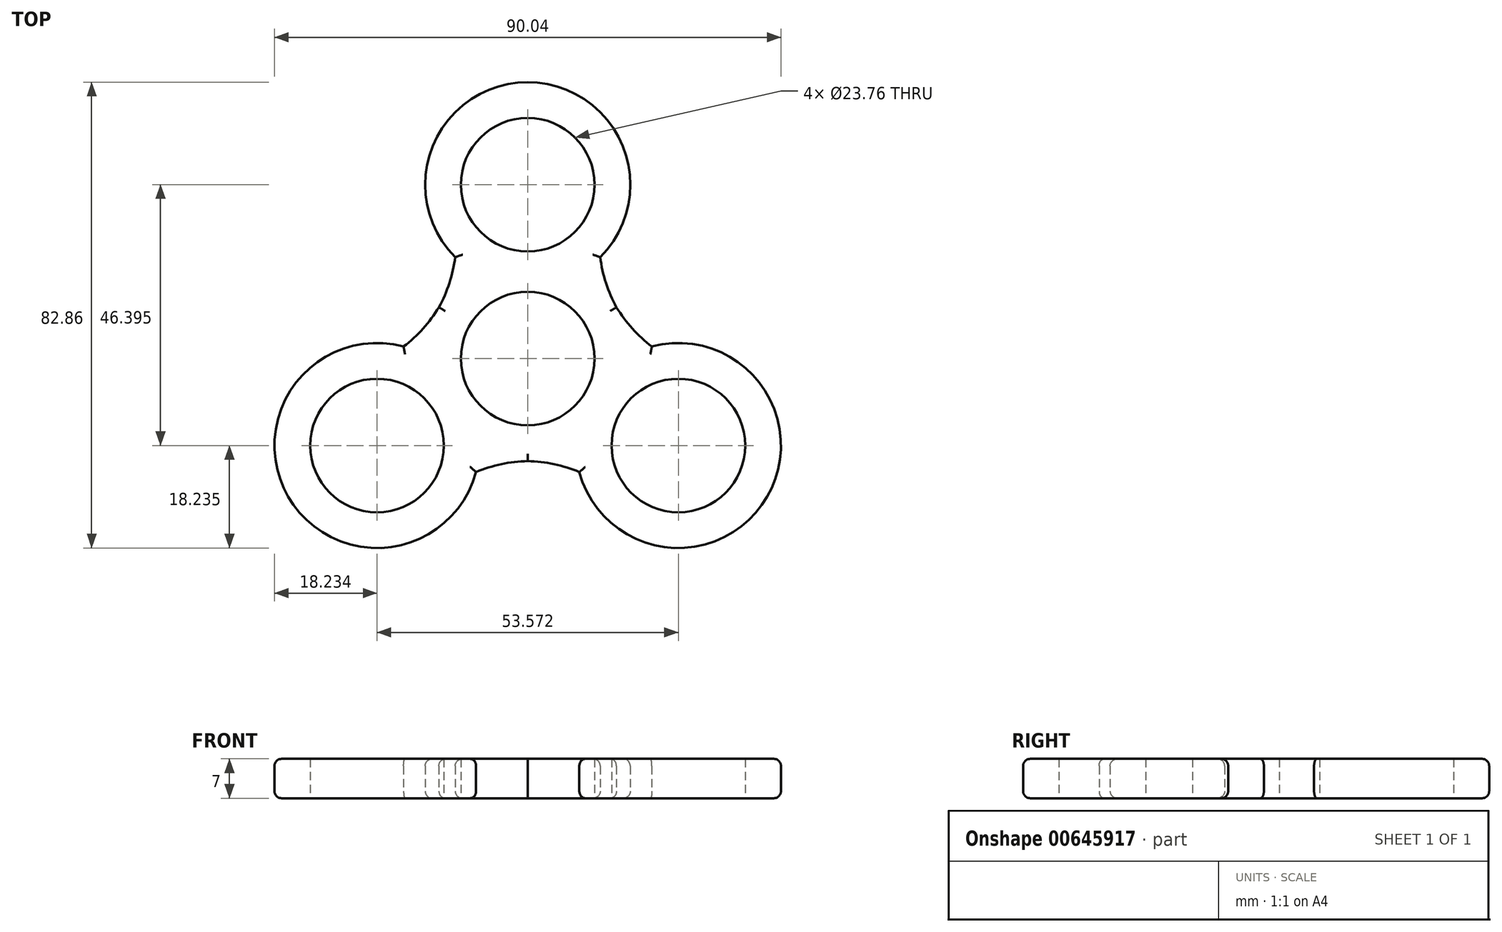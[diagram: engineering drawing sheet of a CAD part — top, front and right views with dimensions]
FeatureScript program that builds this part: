
annotation { "Feature Type Name" : "Feature", "Feature Type Description" : "" }
export const myFeature = defineFeature(function(context is Context, id is Id, definition is map)
    precondition{}
    {
        {
            var Q0;
            Q0=qCreatedBy(makeId("Top.planeOp"),FACE);
            var sketch = newSketch(context, id + "F0", { "sketchPlane" : qUnion([Q0])});
            skCircle(sketch, "E0", {"center": v(0, 0) * mm, "radius": 11.88 * mm});
            skCircle(sketch, "E1", {"center": v(0, 0) * mm, "radius": 18.23 * mm});
            skLineSegment(sketch, "E2", {"start": v(0, 0) * mm, "end": v(0, 18.23) * mm});
            skLineSegment(sketch, "E3", {"start": v(0, 0) * mm, "end": v(15.79, -9.11) * mm});
            skLineSegment(sketch, "E4", {"start": v(0, 0) * mm, "end": v(-15.79, -9.12) * mm});
            skLineSegment(sketch, "E5", {"start": v(0, 18.23) * mm, "end": v(0, 30.93) * mm});
            skCircle(sketch, "E6", {"center": v(0, 30.93) * mm, "radius": 11.88 * mm});
            skCircle(sketch, "E7", {"center": v(0, 30.93) * mm, "radius": 18.23 * mm});
            skLineSegment(sketch, "E8", {"start": v(0, 0) * mm, "end": v(0, -18.23) * mm});
            skLineSegment(sketch, "E9", {"start": v(0, 0) * mm, "end": v(15.79, 9.12) * mm});
            skLineSegment(sketch, "E10", {"start": v(0, 0) * mm, "end": v(-15.79, 9.12) * mm});
            skLineSegment(sketch, "E11", {"start": v(0, 30.93) * mm, "end": v(12.9, 18.04) * mm});
            skLineSegment(sketch, "E12", {"start": v(0, 30.93) * mm, "end": v(-12.9, 18.04) * mm});
            skArc(sketch, "E13", {"start": v(12.9, 18.04) * mm, "mid": v(13.92, 13.44) * mm, "end": v(15.79, 9.11) * mm});
            skArc(sketch, "E14", {"start": v(-15.79, 9.11) * mm, "mid": v(-13.92, 13.44) * mm, "end": v(-12.9, 18.04) * mm});
            skCircle(sketch, "E15.1.0", {"center": v(-26.79, -15.46) * mm, "radius": 11.88 * mm});
            skCircle(sketch, "E15.1.1", {"center": v(-26.79, -15.46) * mm, "radius": 18.23 * mm});
            skArc(sketch, "E15.1.2", {"start": v(-22.07, 2.14) * mm, "mid": v(-18.6, 5.34) * mm, "end": v(-15.79, 9.12) * mm});
            skArc(sketch, "E15.1.3", {"start": v(0, -18.23) * mm, "mid": v(-4.68, -18.78) * mm, "end": v(-9.18, -20.18) * mm});
            skCircle(sketch, "E15.2.0", {"center": v(26.79, -15.46) * mm, "radius": 11.88 * mm});
            skCircle(sketch, "E15.2.1", {"center": v(26.79, -15.46) * mm, "radius": 18.23 * mm});
            skArc(sketch, "E15.2.2", {"start": v(9.18, -20.18) * mm, "mid": v(4.68, -18.78) * mm, "end": v(0, -18.23) * mm});
            skArc(sketch, "E15.2.3", {"start": v(15.79, 9.11) * mm, "mid": v(18.6, 5.34) * mm, "end": v(22.07, 2.14) * mm});
            skSolve(sketch);
        }
        {
            var Q0;
            {var subQ0=sQuery(id+"F0.wireOp",EDGE,"E12");var subQ1=sQuery(id+"F0.wireOp",EDGE,"E6");var subQ2=makeQuery(id+"F0.imprint","INTERSECT",VERTEX,{"derivedFrom":[subQ1,subQ0]});Q0=makeQuery(id+"F0.imprint","IMPRINT",FACE,{"disambiguationData":[TD([[makeQuery(id+"F0.imprint","IMPRINT",EDGE,{"disambiguationData":[TD([[subQ2,1.0]])],"derivedFrom":subQ1}),-1.0]])]});}
            var Q1;
            {var subQ3=sQuery(id+"F0.wireOp",EDGE,"E14");Q1=makeQuery(id+"F0.imprint","IMPRINT",FACE,{"disambiguationData":[TD([[makeQuery(id+"F0.imprint","IMPRINT",EDGE,{"derivedFrom":subQ3}),-1.0]])]});}
            var Q2;
            {var subQ3=sQuery(id+"F0.wireOp",EDGE,"E13");Q2=makeQuery(id+"F0.imprint","IMPRINT",FACE,{"disambiguationData":[TD([[makeQuery(id+"F0.imprint","IMPRINT",EDGE,{"derivedFrom":subQ3}),-1.0]])]});}
            var Q3;
            {var subQ0=sQuery(id+"F0.wireOp",EDGE,"E2");var subQ1=sQuery(id+"F0.wireOp",EDGE,"E0");var subQ2=makeQuery(id+"F0.imprint","INTERSECT",VERTEX,{"derivedFrom":[subQ1,subQ0]});Q3=makeQuery(id+"F0.imprint","IMPRINT",FACE,{"disambiguationData":[TD([[makeQuery(id+"F0.imprint","IMPRINT",EDGE,{"disambiguationData":[TD([[subQ2,1.0]])],"derivedFrom":subQ1}),-1.0]])]});}
            var Q4;
            {var subQ0=sQuery(id+"F0.wireOp",EDGE,"E2");var subQ1=sQuery(id+"F0.wireOp",EDGE,"E0");var subQ2=makeQuery(id+"F0.imprint","INTERSECT",VERTEX,{"derivedFrom":[subQ1,subQ0]});Q4=makeQuery(id+"F0.imprint","IMPRINT",FACE,{"disambiguationData":[TD([[makeQuery(id+"F0.imprint","IMPRINT",EDGE,{"disambiguationData":[TD([[subQ2,-1.0]])],"derivedFrom":subQ1}),-1.0]])]});}
            var Q5;
            {var subQ0=sQuery(id+"F0.wireOp",EDGE,"E10");var subQ1=sQuery(id+"F0.wireOp",EDGE,"E0");var subQ2=makeQuery(id+"F0.imprint","INTERSECT",VERTEX,{"derivedFrom":[subQ1,subQ0]});Q5=makeQuery(id+"F0.imprint","IMPRINT",FACE,{"disambiguationData":[TD([[makeQuery(id+"F0.imprint","IMPRINT",EDGE,{"disambiguationData":[TD([[subQ2,-1.0]])],"derivedFrom":subQ1}),-1.0]])]});}
            var Q6;
            {var subQ0=sQuery(id+"F0.wireOp",EDGE,"E4");var subQ1=sQuery(id+"F0.wireOp",EDGE,"E0");var subQ2=makeQuery(id+"F0.imprint","INTERSECT",VERTEX,{"derivedFrom":[subQ1,subQ0]});Q6=makeQuery(id+"F0.imprint","IMPRINT",FACE,{"disambiguationData":[TD([[makeQuery(id+"F0.imprint","IMPRINT",EDGE,{"disambiguationData":[TD([[subQ2,-1.0]])],"derivedFrom":subQ1}),-1.0]])]});}
            var Q7;
            {var subQ0=sQuery(id+"F0.wireOp",EDGE,"E8");var subQ1=sQuery(id+"F0.wireOp",EDGE,"E0");var subQ2=makeQuery(id+"F0.imprint","INTERSECT",VERTEX,{"derivedFrom":[subQ1,subQ0]});Q7=makeQuery(id+"F0.imprint","IMPRINT",FACE,{"disambiguationData":[TD([[makeQuery(id+"F0.imprint","IMPRINT",EDGE,{"disambiguationData":[TD([[subQ2,-1.0]])],"derivedFrom":subQ1}),-1.0]])]});}
            var Q8;
            {var subQ0=sQuery(id+"F0.wireOp",EDGE,"E9");var subQ1=sQuery(id+"F0.wireOp",EDGE,"E0");var subQ2=makeQuery(id+"F0.imprint","INTERSECT",VERTEX,{"derivedFrom":[subQ1,subQ0]});Q8=makeQuery(id+"F0.imprint","IMPRINT",FACE,{"disambiguationData":[TD([[makeQuery(id+"F0.imprint","IMPRINT",EDGE,{"disambiguationData":[TD([[subQ2,1.0]])],"derivedFrom":subQ1}),-1.0]])]});}
            var Q9;
            {var subQ0=sQuery(id+"F0.wireOp",EDGE,"E15.2.2");Q9=makeQuery(id+"F0.imprint","IMPRINT",FACE,{"disambiguationData":[TD([[makeQuery(id+"F0.imprint","IMPRINT",EDGE,{"derivedFrom":subQ0}),-1.0]])]});}
            var Q10;
            Q10=makeQuery(id+"F0.imprint","IMPRINT",FACE,{"disambiguationData":[TD([[makeQuery(id+"F0.imprint","IMPRINT",EDGE,{"derivedFrom":sQuery(id+"F0.wireOp",EDGE,"E15.2.0")}),-1.0]])]});
            var Q11;
            {var subQ0=sQuery(id+"F0.wireOp",EDGE,"E15.1.2");Q11=makeQuery(id+"F0.imprint","IMPRINT",FACE,{"disambiguationData":[TD([[makeQuery(id+"F0.imprint","IMPRINT",EDGE,{"derivedFrom":subQ0}),-1.0]])]});}
            var Q12;
            Q12=makeQuery(id+"F0.imprint","IMPRINT",FACE,{"disambiguationData":[TD([[makeQuery(id+"F0.imprint","IMPRINT",EDGE,{"derivedFrom":sQuery(id+"F0.wireOp",EDGE,"E15.1.0")}),-1.0]])]});
            var Q13;
            {var subQ5=sQuery(id+"F0.wireOp",EDGE,"E5");var subQ7=sQuery(id+"F0.wireOp",EDGE,"E6");var subQ8=makeQuery(id+"F0.imprint","INTERSECT",VERTEX,{"derivedFrom":[subQ5,subQ7]});Q13=makeQuery(id+"F0.imprint","IMPRINT",FACE,{"disambiguationData":[TD([[makeQuery(id+"F0.imprint","IMPRINT",EDGE,{"disambiguationData":[TD([[subQ8,1.0]])],"derivedFrom":subQ7}),-1.0]])]});}
            var Q14;
            {var subQ5=sQuery(id+"F0.wireOp",EDGE,"E6");var subQ6=sQuery(id+"F0.wireOp",EDGE,"E5");var subQ7=makeQuery(id+"F0.imprint","INTERSECT",VERTEX,{"derivedFrom":[subQ6,subQ5]});Q14=makeQuery(id+"F0.imprint","IMPRINT",FACE,{"disambiguationData":[TD([[makeQuery(id+"F0.imprint","IMPRINT",EDGE,{"disambiguationData":[TD([[subQ7,-1.0]])],"derivedFrom":subQ5}),-1.0]])]});}
            var Q15;
            {var subQ1=sQuery(id+"F0.wireOp",EDGE,"E1");var subQ3=sQuery(id+"F0.wireOp",EDGE,"E7");var subQ4=makeQuery(id+"F0.imprint","INTERSECT",VERTEX,{"disambiguationData":[OD(0.0)],"derivedFrom":[subQ1,subQ3]});Q15=makeQuery(id+"F0.imprint","IMPRINT",FACE,{"disambiguationData":[TD([[makeQuery(id+"F0.imprint","IMPRINT",EDGE,{"disambiguationData":[TD([[subQ4,1.0]])],"derivedFrom":subQ3}),1.0]])]});}
            var Q16;
            {var subQ1=sQuery(id+"F0.wireOp",EDGE,"E1");var subQ3=sQuery(id+"F0.wireOp",EDGE,"E7");var subQ4=makeQuery(id+"F0.imprint","INTERSECT",VERTEX,{"disambiguationData":[OD(1.0)],"derivedFrom":[subQ1,subQ3]});Q16=makeQuery(id+"F0.imprint","IMPRINT",FACE,{"disambiguationData":[TD([[makeQuery(id+"F0.imprint","IMPRINT",EDGE,{"disambiguationData":[TD([[subQ4,-1.0]])],"derivedFrom":subQ3}),1.0]])]});}
            var Q17;
            {var subQ0=sQuery(id+"F0.wireOp",EDGE,"E4");var subQ1=sQuery(id+"F0.wireOp",EDGE,"E1");var subQ2=makeQuery(id+"F0.imprint","INTERSECT",VERTEX,{"derivedFrom":[subQ1,subQ0]});Q17=makeQuery(id+"F0.imprint","IMPRINT",FACE,{"disambiguationData":[TD([[makeQuery(id+"F0.imprint","IMPRINT",EDGE,{"disambiguationData":[TD([[subQ2,1.0]])],"derivedFrom":subQ1}),1.0]])]});}
            var Q18;
            {var subQ0=sQuery(id+"F0.wireOp",EDGE,"E4");var subQ1=sQuery(id+"F0.wireOp",EDGE,"E1");var subQ2=makeQuery(id+"F0.imprint","INTERSECT",VERTEX,{"derivedFrom":[subQ1,subQ0]});Q18=makeQuery(id+"F0.imprint","IMPRINT",FACE,{"disambiguationData":[TD([[makeQuery(id+"F0.imprint","IMPRINT",EDGE,{"disambiguationData":[TD([[subQ2,-1.0]])],"derivedFrom":subQ1}),1.0]])]});}
            var Q19;
            {var subQ0=sQuery(id+"F0.wireOp",EDGE,"E15.1.3");Q19=makeQuery(id+"F0.imprint","IMPRINT",FACE,{"disambiguationData":[TD([[makeQuery(id+"F0.imprint","IMPRINT",EDGE,{"derivedFrom":subQ0}),-1.0]])]});}
            var Q20;
            {var subQ0=sQuery(id+"F0.wireOp",EDGE,"E3");var subQ1=sQuery(id+"F0.wireOp",EDGE,"E1");var subQ2=makeQuery(id+"F0.imprint","INTERSECT",VERTEX,{"derivedFrom":[subQ1,subQ0]});Q20=makeQuery(id+"F0.imprint","IMPRINT",FACE,{"disambiguationData":[TD([[makeQuery(id+"F0.imprint","IMPRINT",EDGE,{"disambiguationData":[TD([[subQ2,1.0]])],"derivedFrom":subQ1}),1.0]])]});}
            var Q21;
            {var subQ0=sQuery(id+"F0.wireOp",EDGE,"E3");var subQ1=sQuery(id+"F0.wireOp",EDGE,"E1");var subQ2=makeQuery(id+"F0.imprint","INTERSECT",VERTEX,{"derivedFrom":[subQ1,subQ0]});Q21=makeQuery(id+"F0.imprint","IMPRINT",FACE,{"disambiguationData":[TD([[makeQuery(id+"F0.imprint","IMPRINT",EDGE,{"disambiguationData":[TD([[subQ2,-1.0]])],"derivedFrom":subQ1}),1.0]])]});}
            var Q22;
            {var subQ0=sQuery(id+"F0.wireOp",EDGE,"E15.2.3");Q22=makeQuery(id+"F0.imprint","IMPRINT",FACE,{"disambiguationData":[TD([[makeQuery(id+"F0.imprint","IMPRINT",EDGE,{"derivedFrom":subQ0}),-1.0]])]});}
            extrude(context, id + "F1", {"entities" : qUnion([Q0, Q1, Q2, Q3, Q4, Q5, Q6, Q7, Q8, Q9, Q10, Q11, Q12, Q13, Q14, Q15, Q16, Q17, Q18, Q19, Q20, Q21, Q22]), "depth" : 7 * mm, "offsetDistance" : 25.4 * mm});
        }
        {
            var Q0;
            Q0=makeQuery(id+"F1.opExtrude","CAP_FACE",FACE,{"disambiguationData":[OSD([sQuery(id+"F0.wireOp",EDGE,"E0"),sQuery(id+"F0.wireOp",EDGE,"E6"),sQuery(id+"F0.wireOp",EDGE,"E7"),sQuery(id+"F0.wireOp",EDGE,"E13"),sQuery(id+"F0.wireOp",EDGE,"E14"),sQuery(id+"F0.wireOp",EDGE,"E15.1.0"),sQuery(id+"F0.wireOp",EDGE,"E15.1.1"),sQuery(id+"F0.wireOp",EDGE,"E15.1.2"),sQuery(id+"F0.wireOp",EDGE,"E15.1.3"),sQuery(id+"F0.wireOp",EDGE,"E15.2.0"),sQuery(id+"F0.wireOp",EDGE,"E15.2.1"),sQuery(id+"F0.wireOp",EDGE,"E15.2.2"),sQuery(id+"F0.wireOp",EDGE,"E15.2.3")])],"isStart":false});
            var Q1;
            Q1=makeQuery(id+"F1.opExtrude","CAP_FACE",FACE,{"disambiguationData":[OSD([sQuery(id+"F0.wireOp",EDGE,"E0"),sQuery(id+"F0.wireOp",EDGE,"E6"),sQuery(id+"F0.wireOp",EDGE,"E7"),sQuery(id+"F0.wireOp",EDGE,"E13"),sQuery(id+"F0.wireOp",EDGE,"E14"),sQuery(id+"F0.wireOp",EDGE,"E15.1.0"),sQuery(id+"F0.wireOp",EDGE,"E15.1.1"),sQuery(id+"F0.wireOp",EDGE,"E15.1.2"),sQuery(id+"F0.wireOp",EDGE,"E15.1.3"),sQuery(id+"F0.wireOp",EDGE,"E15.2.0"),sQuery(id+"F0.wireOp",EDGE,"E15.2.1"),sQuery(id+"F0.wireOp",EDGE,"E15.2.2"),sQuery(id+"F0.wireOp",EDGE,"E15.2.3")])],"isStart":true});
            fillet(context, id + "F2", {"entities" : qUnion([Q0, Q1]), "radius" : 1.27 * mm, "tangentPropagation" : true, "allowEdgeOverflow" : false});
        }
        {
            var Q0;
            Q0=qCreatedBy(makeId("Top.planeOp"),FACE);
            var sketch = newSketch(context, id + "F3", { "sketchPlane" : qUnion([Q0])});
            skCircle(sketch, "E16", {"center": v(0, 0) * mm, "radius": 11.88 * mm});
            skCircle(sketch, "E17", {"center": v(0, 0) * mm, "radius": 16.13 * mm});
            skPoint(sketch, "E18", {"position": v(0, 30.93) * mm});
            skCircle(sketch, "E19", {"center": v(0, 30.93) * mm, "radius": 11.88 * mm});
            skCircle(sketch, "E20", {"center": v(0, 30.93) * mm, "radius": 14.7 * mm});
            skCircle(sketch, "E21.1.0", {"center": v(-26.79, -15.46) * mm, "radius": 14.7 * mm});
            skCircle(sketch, "E21.1.1", {"center": v(-26.79, -15.46) * mm, "radius": 11.88 * mm});
            skCircle(sketch, "E21.2.0", {"center": v(26.79, -15.47) * mm, "radius": 14.7 * mm});
            skCircle(sketch, "E21.2.1", {"center": v(26.79, -15.47) * mm, "radius": 11.88 * mm});
            skSolve(sketch);
        }
        {
            var Q0;
            Q0=makeQuery(id+"F3.imprint","IMPRINT",FACE,{"disambiguationData":[TD([[makeQuery(id+"F3.imprint","IMPRINT",EDGE,{"derivedFrom":sQuery(id+"F3.wireOp",EDGE,"E19")}),-1.0]])]});
            var Q1;
            Q1=makeQuery(id+"F3.imprint","IMPRINT",FACE,{"disambiguationData":[TD([[makeQuery(id+"F3.imprint","IMPRINT",EDGE,{"derivedFrom":sQuery(id+"F3.wireOp",EDGE,"E16")}),-1.0]])]});
            var Q2;
            Q2=makeQuery(id+"F3.imprint","IMPRINT",FACE,{"disambiguationData":[TD([[makeQuery(id+"F3.imprint","IMPRINT",EDGE,{"derivedFrom":sQuery(id+"F3.wireOp",EDGE,"E21.1.0")}),1.0]])]});
            var Q3;
            Q3=makeQuery(id+"F3.imprint","IMPRINT",FACE,{"disambiguationData":[TD([[makeQuery(id+"F3.imprint","IMPRINT",EDGE,{"derivedFrom":sQuery(id+"F3.wireOp",EDGE,"E21.2.0")}),1.0]])]});
            extrude(context, id + "F4", {"entities" : qUnion([Q0, Q1, Q2, Q3]), "operationType" : NewBodyOperationType.ADD, "depth" : 7 * mm, "offsetDistance" : 25.4 * mm});
        }
    });
